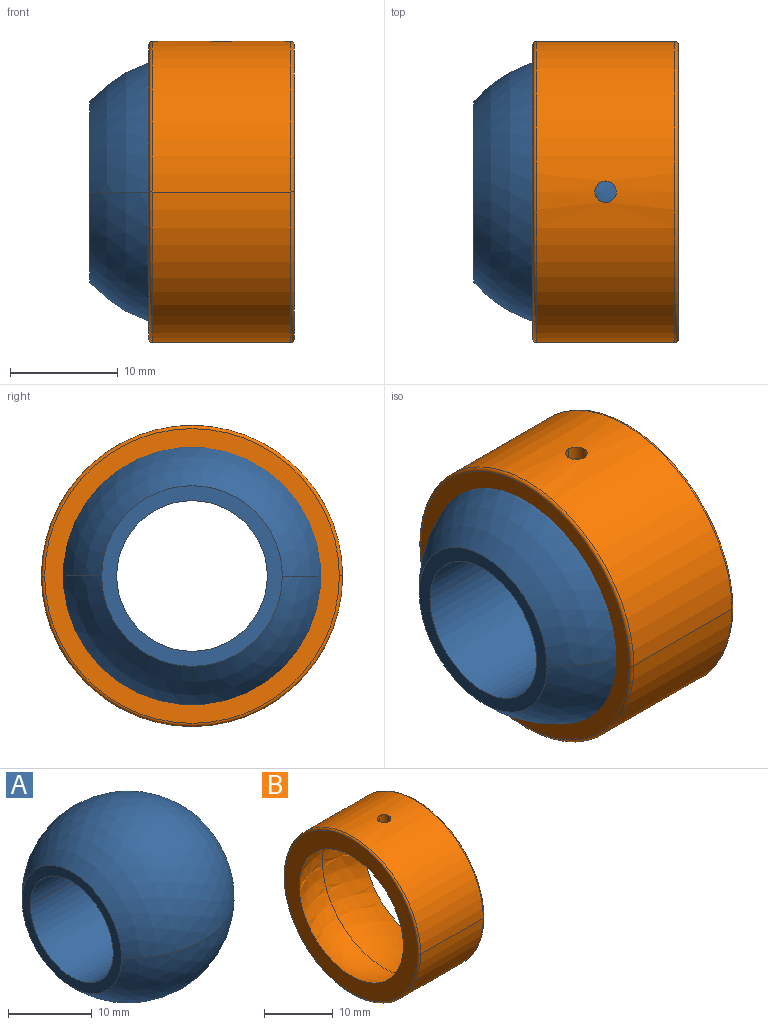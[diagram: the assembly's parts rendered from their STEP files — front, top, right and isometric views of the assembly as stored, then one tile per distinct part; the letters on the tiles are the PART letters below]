
ASSEMBLY  parts=2 mates=1
PART A: 6 faces, bbox 19x25.4x25.4 mm
  f0: plane 16.8x16.8mm, normal (-1,0,0), area 67.6mm2, adj f1,f2,f4,f5
  f1: sphere r=12.68mm, area 756.9mm2, adj f0,f2,f3
  f2: sphere r=12.68mm, area 756.9mm2, adj f0,f1,f3
  f3: plane 16.8x16.8mm, normal (1,0,0), area 67.6mm2, adj f1,f2,f4,f5
  f4: cylinder r=7mm len=19mm, axis (-1,0,0), area 417.8mm2, adj f0,f3,f5
  f5: cylinder r=7mm len=19mm, axis (-1,0,0), area 417.8mm2, adj f0,f3,f4
PART B: 12 faces, bbox 25.4x30.3x30.3 mm
  f0: sphere r=12.68mm, area 536.2mm2, adj f1,f6,f7
  f1: plane 27.4x27.4mm, normal (-1,0,0), area 227.7mm2, adj f0,f2,f3
  f2: torus R=13.7mm, axis (1,0,0), area 20.6mm2, adj f1,f3,f11
  f3: torus R=13.7mm, axis (1,0,0), area 20.6mm2, adj f1,f2,f4
  f4: cylinder r=14mm len=28mm, axis (-1,0,0), area 564.8mm2, adj f3,f5,f6,f10,f11
  f5: cylinder r=1mm len=2mm, axis (0,0,1), area 4.2mm2, adj f4,f6,f7
  f6: cylinder r=1mm len=2mm, axis (0,0,1), area 4.2mm2, adj f0,f4,f5
  f7: sphere r=12.68mm, area 536.2mm2, adj f0,f5,f8
  f8: plane 27.4x27.4mm, normal (1,0,0), area 227.7mm2, adj f7,f9,f10
  f9: torus R=13.7mm, axis (1,0,0), area 20.6mm2, adj f8,f10,f11
  f10: torus R=13.7mm, axis (1,0,0), area 20.6mm2, adj f4,f8,f9
  f11: cylinder r=14mm len=28mm, axis (-1,0,0), area 567.4mm2, adj f2,f4,f9
PLACE A t=(0.06,39.38,5.22)mm
PLACE B t=(2.81,39.38,5.22)mm
MATE ball B.f2 <-> A.f4  axis (1,0,0) through (9.56,39.38,5.22)mm
